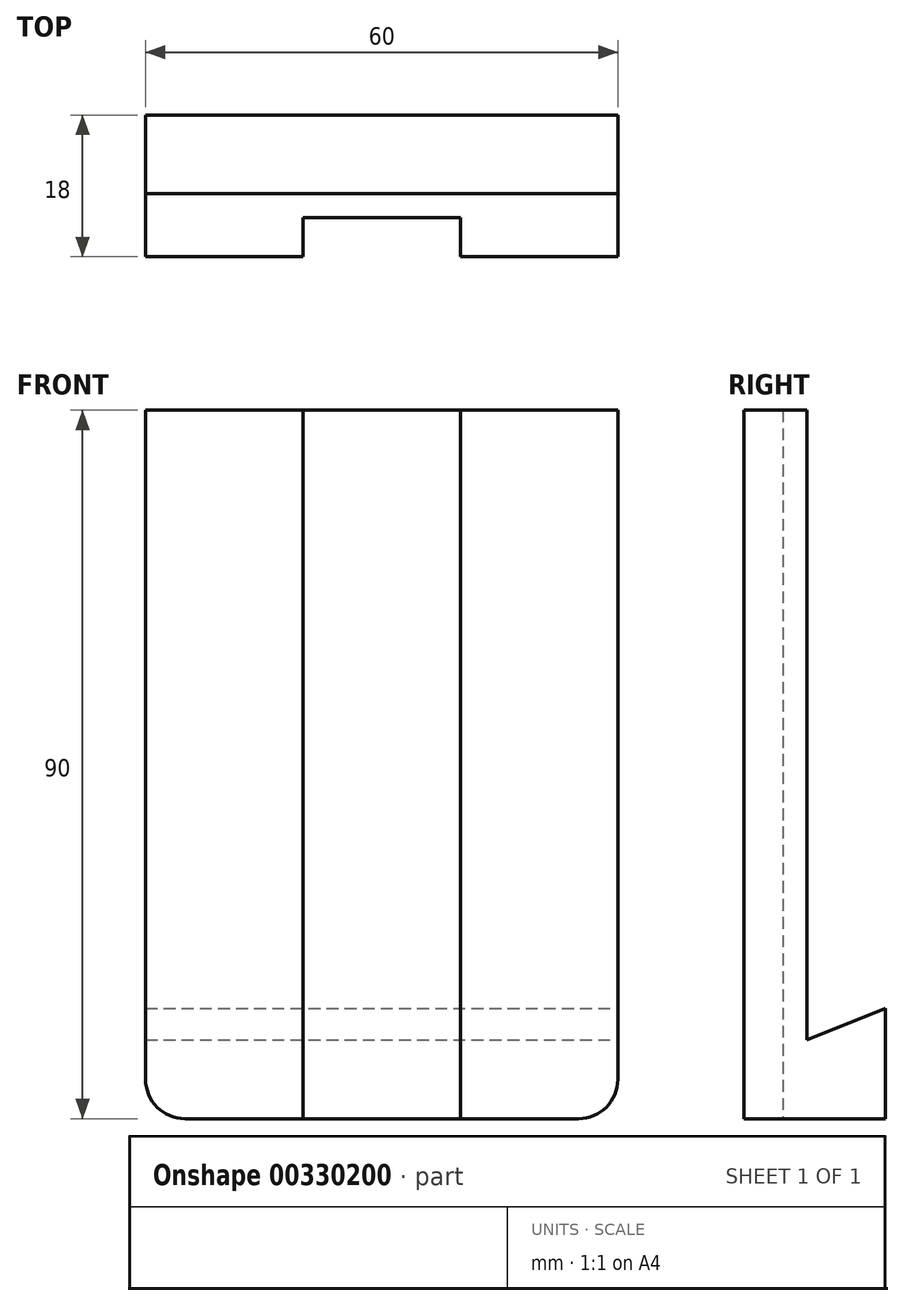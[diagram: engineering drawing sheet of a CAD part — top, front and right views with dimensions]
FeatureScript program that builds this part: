
annotation { "Feature Type Name" : "Feature", "Feature Type Description" : "" }
export const myFeature = defineFeature(function(context is Context, id is Id, definition is map)
    precondition{}
    {
        {
            var Q0;
            Q0=qCreatedBy(makeId("Top.planeOp"),FACE);
            var sketch = newSketch(context, id + "F0", { "sketchPlane" : qUnion([Q0])});
            skLineSegment(sketch, "E0.top", {"start": v(17.49, -21.5) * mm, "end": v(37.49, -21.5) * mm});
            skLineSegment(sketch, "E0.right", {"start": v(37.49, -13.5) * mm, "end": v(37.49, -21.5) * mm});
            skLineSegment(sketch, "E1", {"start": v(17.49, -16.5) * mm, "end": v(17.49, -21.5) * mm});
            skLineSegment(sketch, "E2.MirrorCS", {"start": v(-2.51, -16.5) * mm, "end": v(-2.51, -21.5) * mm});
            skLineSegment(sketch, "E3.MirrorCS", {"start": v(-2.51, -21.5) * mm, "end": v(-22.51, -21.5) * mm});
            skLineSegment(sketch, "E4.MirrorCS", {"start": v(-22.51, -13.5) * mm, "end": v(-22.51, -21.5) * mm});
            skLineSegment(sketch, "E5", {"start": v(-2.51, -16.5) * mm, "end": v(17.49, -16.5) * mm});
            skLineSegment(sketch, "E6", {"start": v(37.49, -13.5) * mm, "end": v(-22.51, -13.5) * mm});
            skLineSegment(sketch, "E7", {"start": v(7.49, -9.3) * mm, "end": v(7.49, -19.8) * mm, "construction": true});
            skPoint(sketch, "E7.startSnap0", {"position": v(7.49, -16.5) * mm});
            skPoint(sketch, "E7.endSnap0", {"position": v(7.49, -13.5) * mm});
            skSolve(sketch);
        }
        {
            var Q0;
            Q0 = qSketchRegion(id + "F0", true);
            extrude(context, id + "F1", {"entities" : qUnion([Q0]), "depth" : 90 * mm});
        }
        {
            var Q0;
            Q0=makeQuery(id+"F1.opExtrude","CAP_EDGE",EDGE,{"disambiguationData":[OSD([sQuery(id+"F0.wireOp",EDGE,"E4.MirrorCS")])],"isStart":true});
            var Q1;
            Q1=makeQuery(id+"F1.opExtrude","CAP_EDGE",EDGE,{"disambiguationData":[OSD([sQuery(id+"F0.wireOp",EDGE,"E0.right")])],"isStart":true});
            fillet(context, id + "F2", {"entities" : qUnion([Q0, Q1]), "radius" : 5 * mm, "tangentPropagation" : true, "allowEdgeOverflow" : false});
        }
        {
            var Q0;
            Q0=makeQuery(id+"F1.opExtrude","SWEPT_FACE",FACE,{"disambiguationData":[OSD([sQuery(id+"F0.wireOp",EDGE,"E6")])]});
            var sketch = newSketch(context, id + "F3", { "sketchPlane" : qUnion([Q0])});
            skLineSegment(sketch, "E8", {"start": v(22.51, 20) * mm, "end": v(-37.49, 20) * mm});
            skSolve(sketch);
        }
        {
            var Q0;
            {var subQ6=sQuery(id+"F3.wireOp",EDGE,"E8");Q0=makeQuery(id+"F3.imprint","IMPRINT",FACE,{"disambiguationData":[TD([[makeQuery(id+"F3.imprint","IMPRINT",EDGE,{"derivedFrom":subQ6}),1.0]])]});}
            extrude(context, id + "F4", {"entities" : qUnion([Q0]), "operationType" : NewBodyOperationType.ADD, "depth" : 10 * mm});
        }
        {
            var Q0;
            {var subQ0=sQuery(id+"F0.wireOp",EDGE,"E6");var subQ1=sQuery(id+"F0.wireOp",EDGE,"E0.right");var subQ2=makeQuery(id+"F1.opExtrude","SWEPT_EDGE",EDGE,{"disambiguationData":[OSD([subQ1,subQ0])]});Q0=makeQuery(id+"F4.boolean.opBoolean","MERGE",FACE,{"derivedFrom":[makeQuery(id+"F1.opExtrude","SWEPT_FACE",FACE,{"disambiguationData":[OSD([subQ1])]}),makeQuery(id+"F4.opExtrude","SWEPT_FACE",FACE,{"disambiguationData":[OSD([subQ1,subQ0]),TDD([makeQuery(id+"F3.imprint","IMPRINT",EDGE,{"disambiguationData":[TD([[makeQuery(id+"F3.imprint","INTERSECT",VERTEX,{"derivedFrom":[subQ2,sQuery(id+"F3.wireOp",EDGE,"E8")]}),-1.0]])],"derivedFrom":subQ2})])]})]});}
            var sketch = newSketch(context, id + "F5", { "sketchPlane" : qUnion([Q0])});
            skLineSegment(sketch, "E9", {"start": v(-3.5, 14.04) * mm, "end": v(-13.5, 10) * mm});
            skLineSegment(sketch, "E10", {"start": v(-13.5, 20) * mm, "end": v(-13.5, 10) * mm});
            skSolve(sketch);
        }
        {
            var Q0;
            {var subQ0=sQuery(id+"F5.wireOp",EDGE,"E9");Q0=makeQuery(id+"F5.imprint","IMPRINT",FACE,{"disambiguationData":[TD([[makeQuery(id+"F5.imprint","IMPRINT",EDGE,{"derivedFrom":subQ0}),-1.0]])]});}
            extrude(context, id + "F6", {"entities" : qUnion([Q0]), "operationType" : NewBodyOperationType.REMOVE, "endBound" : BoundingType.THROUGH_ALL, "oppositeDirection" : true, "depth" : 25 * mm});
        }
    });
